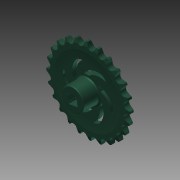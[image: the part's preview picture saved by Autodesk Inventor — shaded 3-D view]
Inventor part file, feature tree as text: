
AUTODESK INVENTOR PART (.ipt)
format: ipt  version: 2013 (Build 170138000, 138)  size: 1,935,872 bytes
history: native  units: mm (DEFAULTED — no unit token found)
features: imported_body x1, sketch x1, other x1, extrude x1
ambient origin geometry x8: Origin, YZ Plane, XZ Plane, XY Plane, X Axis, Y Axis, Z Axis, Center Point
bodies: Solid1 (feature_tree)
feature tree (4):
  imported_body  "Base1"
  sketch  "Sketch1"  dims[d1=2.2606mm d5=25.4mm d6=0.0mm d7=0.0mm d8=0.0mm]
  other  "Srf1"
  extrude  "ExtrusionSrf1"  Depth=25.4mm TaperAngle=0.0deg
